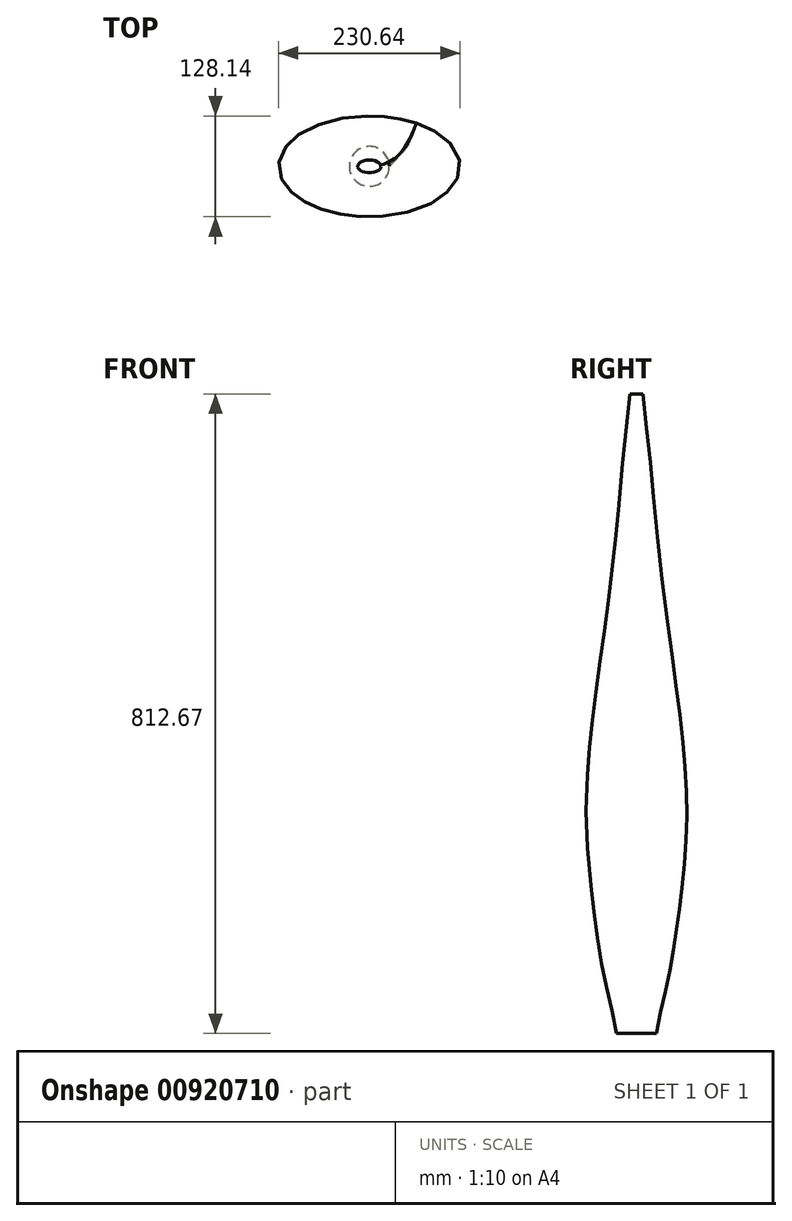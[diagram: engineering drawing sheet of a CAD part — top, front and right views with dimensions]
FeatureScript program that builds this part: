
annotation { "Feature Type Name" : "Feature", "Feature Type Description" : "" }
export const myFeature = defineFeature(function(context is Context, id is Id, definition is map)
    precondition{}
    {
        {
            var Q0;
            Q0=qCreatedBy(makeId("Top.planeOp"),FACE);
            var sketch = newSketch(context, id + "F0", { "sketchPlane" : qUnion([Q0])});
            skEllipse(sketch, "E0", {"center": v(0, 0) * mm, "majorRadius": 25.4 * mm, "minorRadius": 25.4 * mm, "majorAxis": v(1, 0)});
            skSolve(sketch);
        }
        {
            var Q0;
            Q0=qCreatedBy(makeId("Front.planeOp"),FACE);
            var sketch = newSketch(context, id + "F1", { "sketchPlane" : qUnion([Q0])});
            skLineSegment(sketch, "E1", {"start": v(0, 0) * mm, "end": v(0, 90.3) * mm, "construction": true});
            skPoint(sketch, "E2", {"position": v(0, 90.3) * mm});
            skPoint(sketch, "E3.0.1.0", {"position": v(0, 180.6) * mm});
            skPoint(sketch, "E3.0.2.0", {"position": v(0, 270.9) * mm});
            skPoint(sketch, "E3.0.3.0", {"position": v(0, 361.19) * mm});
            skPoint(sketch, "E3.0.4.0", {"position": v(0, 451.49) * mm});
            skPoint(sketch, "E3.0.5.0", {"position": v(0, 541.78) * mm});
            skPoint(sketch, "E3.0.6.0", {"position": v(0, 632.08) * mm});
            skPoint(sketch, "E3.0.7.0", {"position": v(0, 722.38) * mm});
            skPoint(sketch, "E3.0.8.0", {"position": v(0, 812.67) * mm});
            skLineSegment(sketch, "E3.direction1", {"start": v(0, 90.3) * mm, "end": v(25.4, 90.3) * mm, "construction": true});
            skLineSegment(sketch, "E3.direction2", {"start": v(0, 90.3) * mm, "end": v(0, 180.6) * mm, "construction": true});
            skSolve(sketch);
        }
        {
            var Q0;
            Q0=qCreatedBy(makeId("Top.planeOp"),FACE);
            var Q1;
            Q1=sQuery(id+"F1.wireOp",VERTEX,"E2");
            cPlane(context, id + "F2", {"entities" : qUnion([Q0, Q1]), "cplaneType" : CPlaneType.PLANE_POINT, "offset" : 25.4 * mm, "width" : 152.4 * mm, "height" : 152.4 * mm});
        }
        {
            var Q0;
            Q0=qCreatedBy(makeId("Top.planeOp"),FACE);
            var Q1;
            Q1=sQuery(id+"F1.wireOp",VERTEX,"E3.0.1.0");
            cPlane(context, id + "F3", {"entities" : qUnion([Q0, Q1]), "cplaneType" : CPlaneType.PLANE_POINT, "offset" : 25.4 * mm, "width" : 152.4 * mm, "height" : 152.4 * mm});
        }
        {
            var Q0;
            Q0=qCreatedBy(makeId("Top.planeOp"),FACE);
            var Q1;
            Q1=sQuery(id+"F1.wireOp",VERTEX,"E3.0.2.0");
            cPlane(context, id + "F4", {"entities" : qUnion([Q0, Q1]), "cplaneType" : CPlaneType.PLANE_POINT, "offset" : 25.4 * mm, "width" : 152.4 * mm, "height" : 152.4 * mm});
        }
        {
            var Q0;
            Q0=qCreatedBy(makeId("Top.planeOp"),FACE);
            var Q1;
            Q1=sQuery(id+"F1.wireOp",VERTEX,"E3.0.3.0");
            cPlane(context, id + "F5", {"entities" : qUnion([Q0, Q1]), "cplaneType" : CPlaneType.PLANE_POINT, "offset" : 25.4 * mm, "width" : 152.4 * mm, "height" : 152.4 * mm});
        }
        {
            var Q0;
            Q0=qCreatedBy(makeId("Top.planeOp"),FACE);
            var Q1;
            Q1=sQuery(id+"F1.wireOp",VERTEX,"E3.0.4.0");
            cPlane(context, id + "F6", {"entities" : qUnion([Q0, Q1]), "cplaneType" : CPlaneType.PLANE_POINT, "offset" : 25.4 * mm, "width" : 152.4 * mm, "height" : 152.4 * mm});
        }
        {
            var Q0;
            Q0=qCreatedBy(makeId("Top.planeOp"),FACE);
            var Q1;
            Q1=sQuery(id+"F1.wireOp",VERTEX,"E3.0.5.0");
            cPlane(context, id + "F7", {"entities" : qUnion([Q0, Q1]), "cplaneType" : CPlaneType.PLANE_POINT, "offset" : 25.4 * mm, "width" : 152.4 * mm, "height" : 152.4 * mm});
        }
        {
            var Q0;
            Q0=qCreatedBy(makeId("Top.planeOp"),FACE);
            var Q1;
            Q1=sQuery(id+"F1.wireOp",VERTEX,"E3.0.6.0");
            cPlane(context, id + "F8", {"entities" : qUnion([Q0, Q1]), "cplaneType" : CPlaneType.PLANE_POINT, "offset" : 25.4 * mm, "width" : 152.4 * mm, "height" : 152.4 * mm});
        }
        {
            var Q0;
            Q0=qCreatedBy(makeId("Top.planeOp"),FACE);
            var Q1;
            Q1=sQuery(id+"F1.wireOp",VERTEX,"E3.0.7.0");
            cPlane(context, id + "F9", {"entities" : qUnion([Q0, Q1]), "cplaneType" : CPlaneType.PLANE_POINT, "offset" : 25.4 * mm, "width" : 152.4 * mm, "height" : 152.4 * mm});
        }
        {
            var Q0;
            Q0=qCreatedBy(makeId("Top.planeOp"),FACE);
            var Q1;
            Q1=sQuery(id+"F1.wireOp",VERTEX,"E3.0.8.0");
            cPlane(context, id + "F10", {"entities" : qUnion([Q0, Q1]), "cplaneType" : CPlaneType.PLANE_POINT, "offset" : 25.4 * mm, "width" : 152.4 * mm, "height" : 152.4 * mm});
        }
        {
            var Q0;
            Q0=qCreatedBy(id+"F2.planeOp",FACE);
            var sketch = newSketch(context, id + "F11", { "sketchPlane" : qUnion([Q0])});
            skEllipse(sketch, "E4", {"center": v(0, 0) * mm, "majorRadius": 63.5 * mm, "minorRadius": 44.45 * mm, "majorAxis": v(1, 0)});
            skSolve(sketch);
        }
        {
            var Q0;
            Q0=qCreatedBy(id+"F3.planeOp",FACE);
            var sketch = newSketch(context, id + "F12", { "sketchPlane" : qUnion([Q0])});
            skEllipse(sketch, "E5", {"center": v(0, 0) * mm, "majorRadius": 102.74 * mm, "minorRadius": 57.15 * mm, "majorAxis": v(1, 0)});
            skSolve(sketch);
        }
        {
            var Q0;
            Q0=qCreatedBy(id+"F4.planeOp",FACE);
            var sketch = newSketch(context, id + "F13", { "sketchPlane" : qUnion([Q0])});
            skEllipse(sketch, "E6", {"center": v(0, 0) * mm, "majorRadius": 115.32 * mm, "minorRadius": 64 * mm, "majorAxis": v(1, 0)});
            skSolve(sketch);
        }
        {
            var Q0;
            Q0=qCreatedBy(id+"F5.planeOp",FACE);
            var sketch = newSketch(context, id + "F14", { "sketchPlane" : qUnion([Q0])});
            skEllipse(sketch, "E7", {"center": v(0, 0) * mm, "majorRadius": 107.44 * mm, "minorRadius": 59.7 * mm, "majorAxis": v(1, 0)});
            skSolve(sketch);
        }
        {
            var Q0;
            Q0=qCreatedBy(id+"F6.planeOp",FACE);
            var sketch = newSketch(context, id + "F15", { "sketchPlane" : qUnion([Q0])});
            skEllipse(sketch, "E8", {"center": v(0, 0) * mm, "majorRadius": 88.52 * mm, "minorRadius": 49.15 * mm, "majorAxis": v(1, 0)});
            skSolve(sketch);
        }
        {
            var Q0;
            Q0=qCreatedBy(id+"F7.planeOp",FACE);
            var sketch = newSketch(context, id + "F16", { "sketchPlane" : qUnion([Q0])});
            skEllipse(sketch, "E9", {"center": v(0, 0) * mm, "majorRadius": 66.3 * mm, "minorRadius": 36.83 * mm, "majorAxis": v(1, 0)});
            skSolve(sketch);
        }
        {
            var Q0;
            Q0=qCreatedBy(id+"F8.planeOp",FACE);
            var sketch = newSketch(context, id + "F17", { "sketchPlane" : qUnion([Q0])});
            skEllipse(sketch, "E10", {"center": v(0, 0) * mm, "majorRadius": 47.5 * mm, "minorRadius": 26.42 * mm, "majorAxis": v(1, 0)});
            skSolve(sketch);
        }
        {
            var Q0;
            Q0=qCreatedBy(id+"F9.planeOp",FACE);
            var sketch = newSketch(context, id + "F18", { "sketchPlane" : qUnion([Q0])});
            skEllipse(sketch, "E11", {"center": v(0, 0) * mm, "majorRadius": 31.75 * mm, "minorRadius": 17.78 * mm, "majorAxis": v(1, 0)});
            skSolve(sketch);
        }
        {
            var Q0;
            Q0=qCreatedBy(id+"F10.planeOp",FACE);
            var sketch = newSketch(context, id + "F19", { "sketchPlane" : qUnion([Q0])});
            skEllipse(sketch, "E12", {"center": v(0, 0) * mm, "majorRadius": 14.73 * mm, "minorRadius": 8.13 * mm, "majorAxis": v(1, 0)});
            skSolve(sketch);
        }
        {
            var Q0;
            Q0=makeQuery(id+"F0.imprint","IMPRINT",FACE,{"disambiguationData":[TD([[makeQuery(id+"F0.imprint","IMPRINT",EDGE,{"derivedFrom":sQuery(id+"F0.wireOp",EDGE,"E0")}),1.0]])]});
            var Q1;
            Q1=makeQuery(id+"F11.imprint","IMPRINT",FACE,{"disambiguationData":[TD([[makeQuery(id+"F11.imprint","IMPRINT",EDGE,{"derivedFrom":sQuery(id+"F11.wireOp",EDGE,"E4")}),1.0]])]});
            var Q2;
            Q2=makeQuery(id+"F12.imprint","IMPRINT",FACE,{"disambiguationData":[TD([[makeQuery(id+"F12.imprint","IMPRINT",EDGE,{"derivedFrom":sQuery(id+"F12.wireOp",EDGE,"E5")}),1.0]])]});
            var Q3;
            Q3=makeQuery(id+"F13.imprint","IMPRINT",FACE,{"disambiguationData":[TD([[makeQuery(id+"F13.imprint","IMPRINT",EDGE,{"derivedFrom":sQuery(id+"F13.wireOp",EDGE,"E6")}),1.0]])]});
            var Q4;
            Q4=makeQuery(id+"F14.imprint","IMPRINT",FACE,{"disambiguationData":[TD([[makeQuery(id+"F14.imprint","IMPRINT",EDGE,{"derivedFrom":sQuery(id+"F14.wireOp",EDGE,"E7")}),1.0]])]});
            var Q5;
            Q5=makeQuery(id+"F15.imprint","IMPRINT",FACE,{"disambiguationData":[TD([[makeQuery(id+"F15.imprint","IMPRINT",EDGE,{"derivedFrom":sQuery(id+"F15.wireOp",EDGE,"E8")}),1.0]])]});
            var Q6;
            Q6=makeQuery(id+"F16.imprint","IMPRINT",FACE,{"disambiguationData":[TD([[makeQuery(id+"F16.imprint","IMPRINT",EDGE,{"derivedFrom":sQuery(id+"F16.wireOp",EDGE,"E9")}),1.0]])]});
            var Q7;
            Q7=makeQuery(id+"F17.imprint","IMPRINT",FACE,{"disambiguationData":[TD([[makeQuery(id+"F17.imprint","IMPRINT",EDGE,{"derivedFrom":sQuery(id+"F17.wireOp",EDGE,"E10")}),1.0]])]});
            var Q8;
            Q8=makeQuery(id+"F18.imprint","IMPRINT",FACE,{"disambiguationData":[TD([[makeQuery(id+"F18.imprint","IMPRINT",EDGE,{"derivedFrom":sQuery(id+"F18.wireOp",EDGE,"E11")}),1.0]])]});
            var Q9;
            Q9=makeQuery(id+"F19.imprint","IMPRINT",FACE,{"disambiguationData":[TD([[makeQuery(id+"F19.imprint","IMPRINT",EDGE,{"derivedFrom":sQuery(id+"F19.wireOp",EDGE,"E12")}),1.0]])]});
            loft(context, id + "F20", {"sheetProfilesArray" : [{ "sheetProfileEntities" : qUnion([Q0]) }, { "sheetProfileEntities" : qUnion([Q1]) }, { "sheetProfileEntities" : qUnion([Q2]) }, { "sheetProfileEntities" : qUnion([Q3]) }, { "sheetProfileEntities" : qUnion([Q4]) }, { "sheetProfileEntities" : qUnion([Q5]) }, { "sheetProfileEntities" : qUnion([Q6]) }, { "sheetProfileEntities" : qUnion([Q7]) }, { "sheetProfileEntities" : qUnion([Q8]) }, { "sheetProfileEntities" : qUnion([Q9]) }]});
        }
    });
